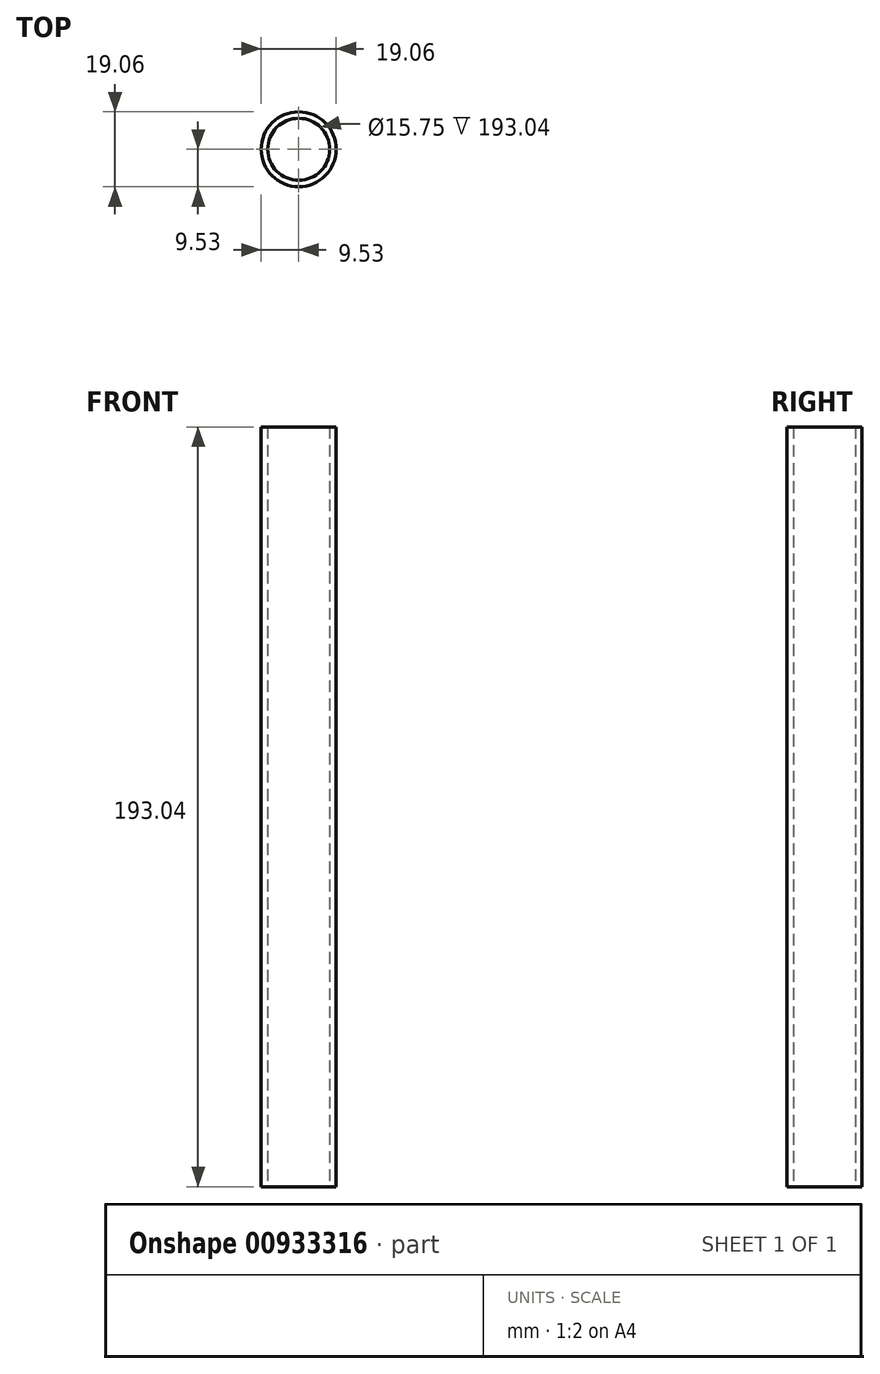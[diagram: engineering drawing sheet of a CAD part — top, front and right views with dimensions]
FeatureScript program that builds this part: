
annotation { "Feature Type Name" : "Feature", "Feature Type Description" : "" }
export const myFeature = defineFeature(function(context is Context, id is Id, definition is map)
    precondition{}
    {
        {
            var Q0;
            Q0=qCreatedBy(makeId("Top.planeOp"),FACE);
            var sketch = newSketch(context, id + "F0", { "sketchPlane" : qUnion([Q0])});
            skCircle(sketch, "E0", {"center": v(0, 0) * mm, "radius": 9.53 * mm});
            skCircle(sketch, "E1", {"center": v(0, 0) * mm, "radius": 7.87 * mm});
            skSolve(sketch);
        }
        {
            var Q0;
            Q0=makeQuery(id+"F0.imprint","IMPRINT",FACE,{"disambiguationData":[TD([[makeQuery(id+"F0.imprint","IMPRINT",EDGE,{"derivedFrom":sQuery(id+"F0.wireOp",EDGE,"E0")}),1.0]])]});
            extrude(context, id + "F1", {"entities" : qUnion([Q0]), "depth" : 193.04 * mm, "offsetDistance" : 25.4 * mm});
        }
    });
